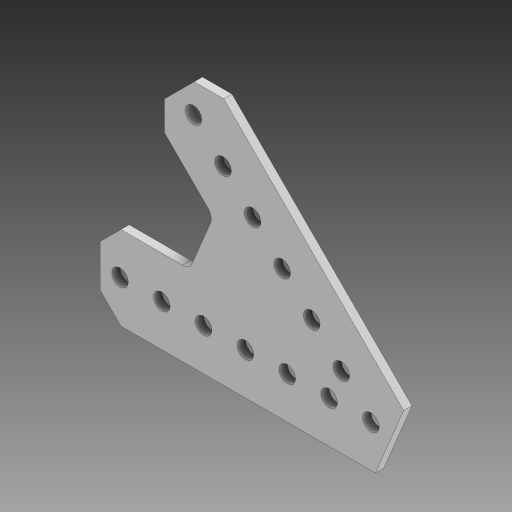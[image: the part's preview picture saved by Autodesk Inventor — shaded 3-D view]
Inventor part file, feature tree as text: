
AUTODESK INVENTOR PART (.ipt)
format: ipt  version: 2023.4 (Build 274418000, 418)  size: 136,704 bytes
history: native  units: in
note: dims shown in document units (in); Inventor stores cm internally (conversion verified against a paired STEP export)
features: fillet x1
ambient origin geometry x8: Origin, YZ Plane, XZ Plane, XY Plane, X Axis, Y Axis, Z Axis, Center Point
bodies: Solid1 (feature_tree)
feature tree (1):
  fillet  "Fillet1"  [1 undecoded]
note: 1 required parameter value undecoded (feature->parameter linkage not recoverable at this tier; creation-order binding heuristic only, values carry confidence <= 0.55)
